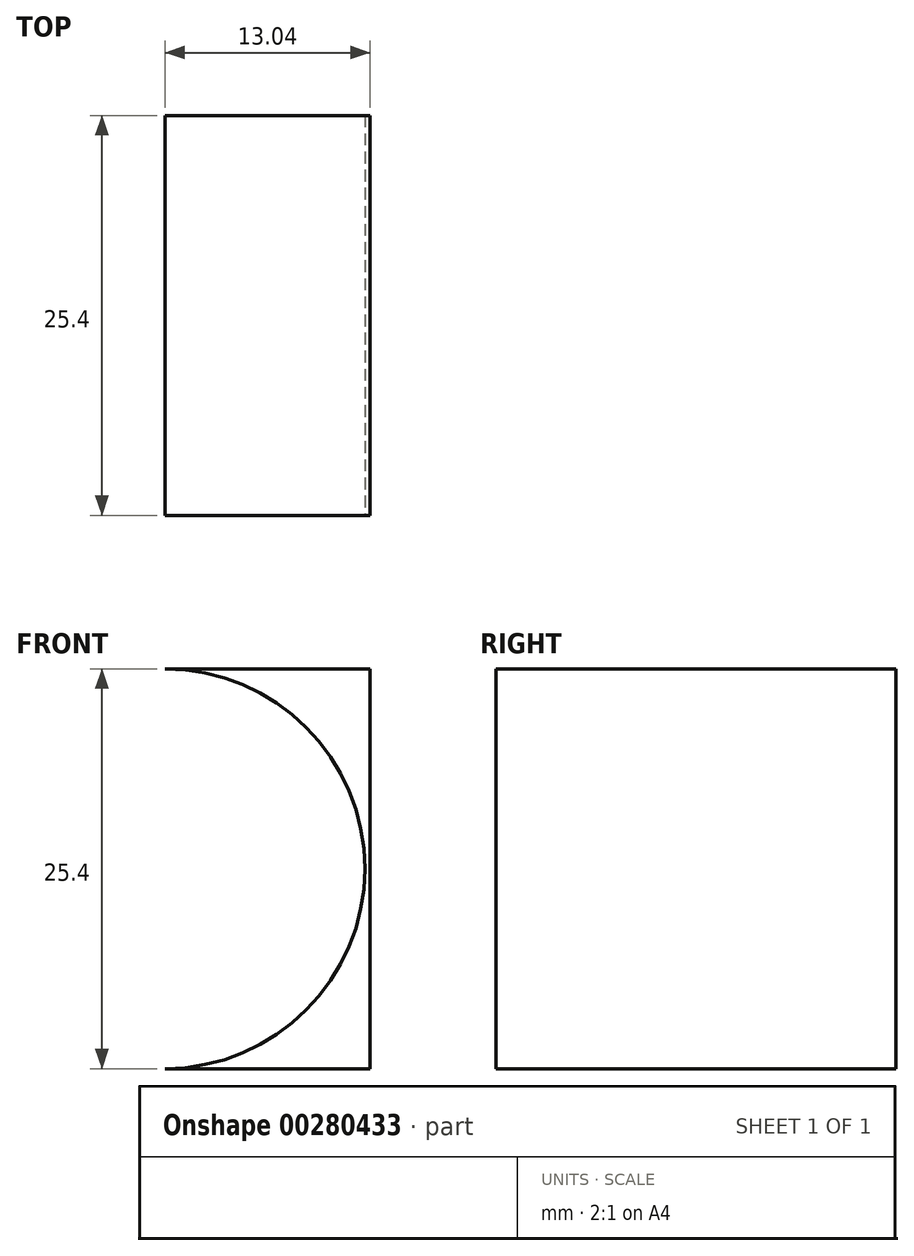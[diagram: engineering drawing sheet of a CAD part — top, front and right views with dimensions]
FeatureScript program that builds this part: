
annotation { "Feature Type Name" : "Feature", "Feature Type Description" : "" }
export const myFeature = defineFeature(function(context is Context, id is Id, definition is map)
    precondition{}
    {
        {
            var Q0;
            Q0=qCreatedBy(makeId("Front.planeOp"),FACE);
            var sketch = newSketch(context, id + "F0", { "sketchPlane" : qUnion([Q0])});
            skLineSegment(sketch, "E0", {"start": v(0, 0) * mm, "end": v(38.1, 0) * mm});
            skLineSegment(sketch, "E1", {"start": v(38.1, 0) * mm, "end": v(38.1, 25.4) * mm});
            skLineSegment(sketch, "E2", {"start": v(38.1, 25.4) * mm, "end": v(0, 25.4) * mm});
            skLineSegment(sketch, "E3", {"start": v(0, 25.4) * mm, "end": v(0, 0) * mm});
            skSolve(sketch);
        }
        {
            var Q0;
            Q0=qSketchRegion(id+"F0",true);
            extrude(context, id + "F1", {"entities" : qUnion([Q0]), "endBound" : BoundingType.SYMMETRIC, "depth" : 25.4 * mm});
        }
        {
            var Q0;
            Q0=makeQuery(id+"F1.opExtrude","CAP_FACE",FACE,{"disambiguationData":[OSD([sQuery(id+"F0.wireOp",EDGE,"E0"),sQuery(id+"F0.wireOp",EDGE,"E1"),sQuery(id+"F0.wireOp",EDGE,"E2"),sQuery(id+"F0.wireOp",EDGE,"E3")])],"isStart":false});
            var sketch = newSketch(context, id + "F2", { "sketchPlane" : qUnion([Q0])});
            skPoint(sketch, "E4", {"position": v(0, 12.7) * mm});
            skArc(sketch, "E5", {"start": v(25.06, 25.4) * mm, "mid": v(37.76, 12.7) * mm, "end": v(25.06, 0) * mm});
            skLineSegment(sketch, "E6", {"start": v(25.06, 25.4) * mm, "end": v(38.1, 25.4) * mm});
            skLineSegment(sketch, "E7", {"start": v(38.1, 25.4) * mm, "end": v(38.1, 0) * mm});
            skLineSegment(sketch, "E8", {"start": v(38.1, 0) * mm, "end": v(25.06, 0) * mm});
            skSolve(sketch);
        }
        {
            var Q0;
            Q0=makeQuery(id+"F2.imprint","IMPRINT",FACE,{"disambiguationData":[TD([[makeQuery(id+"F2.imprint","IMPRINT",EDGE,{"derivedFrom":sQuery(id+"F2.wireOp",EDGE,"E5")}),1.0]])]});
            extrude(context, id + "F3", {"entities" : qUnion([Q0]), "operationType" : NewBodyOperationType.REMOVE, "endBound" : BoundingType.THROUGH_ALL, "oppositeDirection" : true, "depth" : 25.4 * mm});
        }
        {
            var Q0;
            Q0=makeQuery(id+"F1.opExtrude","SWEPT_FACE",FACE,{"disambiguationData":[OSD([sQuery(id+"F0.wireOp",EDGE,"E2")])]});
            var sketch = newSketch(context, id + "F4", { "sketchPlane" : qUnion([Q0])});
            skLineSegment(sketch, "E9", {"start": v(12.53, -12.7) * mm, "end": v(12.53, 0) * mm});
            skLineSegment(sketch, "E10", {"start": v(12.53, 0) * mm, "end": v(38.24, 0) * mm});
            skLineSegment(sketch, "E11", {"start": v(38.24, 0) * mm, "end": v(38.24, -12.7) * mm});
            skLineSegment(sketch, "E12", {"start": v(38.24, -12.7) * mm, "end": v(12.53, -12.7) * mm});
            skSolve(sketch);
        }
        {
            var Q0;
            {var subQ0=sQuery(id+"F4.wireOp",EDGE,"E9");Q0=makeQuery(id+"F4.imprint","IMPRINT",FACE,{"disambiguationData":[TD([[makeQuery(id+"F4.imprint","IMPRINT",EDGE,{"derivedFrom":subQ0}),-1.0]])]});}
            var Q1;
            {var subQ0=sQuery(id+"F4.wireOp",EDGE,"E11");Q1=makeQuery(id+"F4.imprint","IMPRINT",FACE,{"disambiguationData":[TD([[makeQuery(id+"F4.imprint","IMPRINT",EDGE,{"derivedFrom":subQ0}),-1.0]])]});}
            extrude(context, id + "F5", {"entities" : qUnion([Q0, Q1]), "operationType" : NewBodyOperationType.REMOVE, "endBound" : BoundingType.THROUGH_ALL, "oppositeDirection" : true, "depth" : 25.4 * mm});
        }
        {
            var Q0;
            {var subQ0=sQuery(id+"F2.wireOp",EDGE,"E5");Q0=makeQuery(id+"F2.imprint","IMPRINT",FACE,{"disambiguationData":[TD([[makeQuery(id+"F2.imprint","IMPRINT",EDGE,{"derivedFrom":subQ0}),-1.0]])]});}
            var sketch = newSketch(context, id + "F6", { "sketchPlane" : qUnion([Q0])});
            skLineSegment(sketch, "E13", {"start": v(0, 19.7) * mm, "end": v(12.5, 19.7) * mm});
            skLineSegment(sketch, "E14", {"start": v(12.5, 19.7) * mm, "end": v(12.5, 5.94) * mm});
            skLineSegment(sketch, "E15", {"start": v(12.5, 5.94) * mm, "end": v(0, 5.94) * mm});
            skLineSegment(sketch, "E16", {"start": v(0, 5.94) * mm, "end": v(0, 19.7) * mm});
            skSolve(sketch);
        }
        {
            var Q0;
            Q0 = qSketchRegion(id + "F6", true);
            extrude(context, id + "F7", {"entities" : qUnion([Q0]), "operationType" : NewBodyOperationType.REMOVE, "oppositeDirection" : true, "depth" : 12.7 * mm});
        }
        {
            var Q0;
            Q0=makeQuery(id+"F0.imprint","IMPRINT",FACE,{"disambiguationData":[TD([[makeQuery(id+"F0.imprint","IMPRINT",EDGE,{"derivedFrom":sQuery(id+"F0.wireOp",EDGE,"E0")}),1.0]])]});
            var sketch = newSketch(context, id + "F8", { "sketchPlane" : qUnion([Q0])});
            skCircle(sketch, "E17", {"center": v(26.07, 12.6) * mm, "radius": 6.78 * mm});
            skSolve(sketch);
        }
        {
            var Q0;
            Q0=makeQuery(id+"F8.imprint","IMPRINT",FACE,{"disambiguationData":[TD([[makeQuery(id+"F8.imprint","IMPRINT",EDGE,{"derivedFrom":sQuery(id+"F8.wireOp",EDGE,"E17")}),1.0]])]});
            extrude(context, id + "F9", {"entities" : qUnion([Q0]), "operationType" : NewBodyOperationType.REMOVE, "endBound" : BoundingType.THROUGH_ALL, "oppositeDirection" : true, "depth" : 25.4 * mm});
        }
    });
